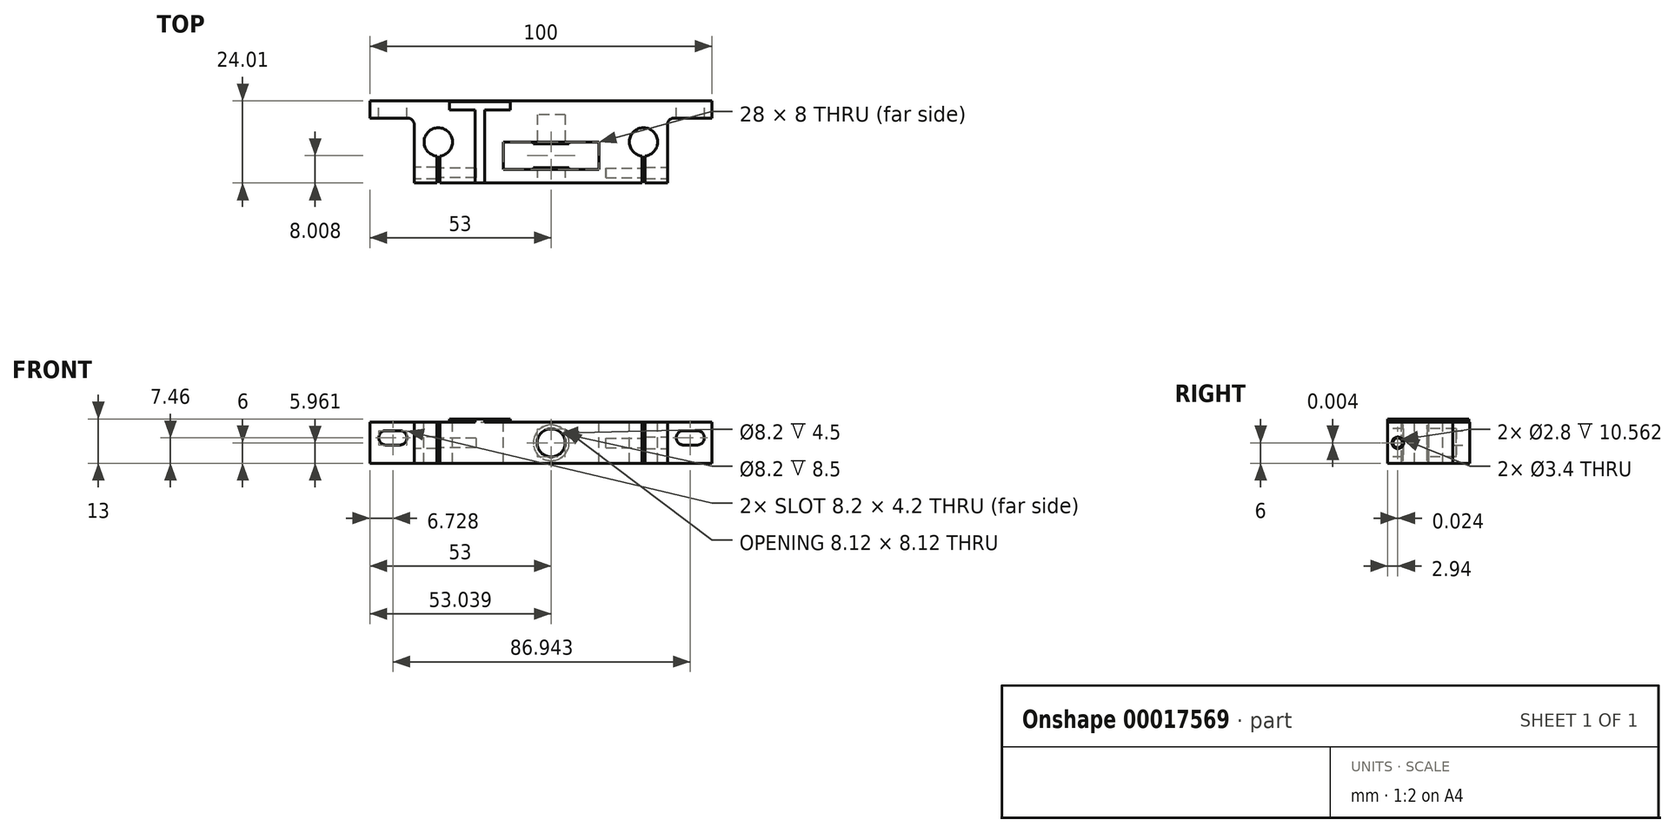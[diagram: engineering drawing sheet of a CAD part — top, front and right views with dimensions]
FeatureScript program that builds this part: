
annotation { "Feature Type Name" : "Feature", "Feature Type Description" : "" }
export const myFeature = defineFeature(function(context is Context, id is Id, definition is map)
    precondition{}
    {
        {
            var Q0;
            Q0=qCreatedBy(makeId("Top.planeOp"),FACE);
            var sketch = newSketch(context, id + "F0", { "sketchPlane" : qUnion([Q0])});
            skLineSegment(sketch, "E0", {"start": v(-46.35, 12.3) * mm, "end": v(53.65, 12.3) * mm});
            skLineSegment(sketch, "E1", {"start": v(53.65, 12.3) * mm, "end": v(53.65, 7.3) * mm});
            skLineSegment(sketch, "E2", {"start": v(53.65, 7.3) * mm, "end": v(40.65, 7.3) * mm});
            skLineSegment(sketch, "E3", {"start": v(40.65, 7.3) * mm, "end": v(40.65, -11.7) * mm});
            skLineSegment(sketch, "E4", {"start": v(40.65, -11.7) * mm, "end": v(-33.35, -11.7) * mm});
            skLineSegment(sketch, "E5", {"start": v(-33.35, -11.7) * mm, "end": v(-33.35, 7.3) * mm});
            skLineSegment(sketch, "E6", {"start": v(-33.35, 7.3) * mm, "end": v(-46.35, 7.3) * mm});
            skLineSegment(sketch, "E7", {"start": v(-46.35, 7.3) * mm, "end": v(-46.35, 12.3) * mm});
            skSolve(sketch);
        }
        {
            var Q0;
            Q0=qSketchRegion(id+"F0",true);
            extrude(context, id + "F1", {"entities" : qUnion([Q0]), "depth" : 12 * mm});
        }
        {
            var Q0;
            Q0=makeQuery(id+"F1.opExtrude","CAP_FACE",FACE,{"disambiguationData":[OSD([sQuery(id+"F0.wireOp",EDGE,"E0"),sQuery(id+"F0.wireOp",EDGE,"E1"),sQuery(id+"F0.wireOp",EDGE,"E2"),sQuery(id+"F0.wireOp",EDGE,"E3"),sQuery(id+"F0.wireOp",EDGE,"E4"),sQuery(id+"F0.wireOp",EDGE,"E5"),sQuery(id+"F0.wireOp",EDGE,"E6"),sQuery(id+"F0.wireOp",EDGE,"E7")])],"isStart":false});
            var sketch = newSketch(context, id + "F2", { "sketchPlane" : qUnion([Q0])});
            skCircle(sketch, "E8", {"center": v(-26.35, 0.3) * mm, "radius": 4.15 * mm});
            skCircle(sketch, "E9", {"center": v(33.65, 0.3) * mm, "radius": 4.15 * mm});
            skPoint(sketch, "E10", {"position": v(3.65, 12.3) * mm});
            skLineSegment(sketch, "E11.bottom", {"start": v(33.21, -3.01) * mm, "end": v(34.09, -3.01) * mm});
            skLineSegment(sketch, "E11.top", {"start": v(33.21, -12.27) * mm, "end": v(34.09, -12.27) * mm});
            skLineSegment(sketch, "E11.left", {"start": v(33.21, -3.01) * mm, "end": v(33.21, -12.27) * mm});
            skLineSegment(sketch, "E11.right", {"start": v(34.09, -3.01) * mm, "end": v(34.09, -12.27) * mm});
            skPoint(sketch, "E12", {"position": v(33.65, -3.01) * mm});
            skLineSegment(sketch, "E13", {"start": v(3.65, 12.3) * mm, "end": v(3.65, -11.7) * mm, "construction": true});
            skLineSegment(sketch, "E14.MirrorCS", {"start": v(-25.91, -12.27) * mm, "end": v(-26.79, -12.27) * mm});
            skLineSegment(sketch, "E15.MirrorCS", {"start": v(-26.79, -3.01) * mm, "end": v(-26.79, -12.27) * mm});
            skLineSegment(sketch, "E16.MirrorCS", {"start": v(-25.91, -3.01) * mm, "end": v(-26.79, -3.01) * mm});
            skLineSegment(sketch, "E17.MirrorCS", {"start": v(-25.91, -3.01) * mm, "end": v(-25.91, -12.27) * mm});
            skSolve(sketch);
        }
        {
            var Q0;
            Q0=qSketchRegion(id+"F2",true);
            var Q1;
            {var subQ3=sQuery(id+"F2.wireOp",EDGE,"E11.bottom");Q1=makeQuery(id+"F2.imprint","IMPRINT",FACE,{"disambiguationData":[TD([[makeQuery(id+"F2.imprint","IMPRINT",EDGE,{"derivedFrom":subQ3}),-1.0]])]});}
            var Q2;
            {var subQ3=sQuery(id+"F2.wireOp",EDGE,"E16.MirrorCS");Q2=makeQuery(id+"F2.imprint","IMPRINT",FACE,{"disambiguationData":[TD([[makeQuery(id+"F2.imprint","IMPRINT",EDGE,{"derivedFrom":subQ3}),1.0]])]});}
            extrude(context, id + "F3", {"entities" : qUnion([Q0, Q1, Q2]), "operationType" : NewBodyOperationType.REMOVE, "endBound" : BoundingType.THROUGH_ALL, "oppositeDirection" : true, "depth" : 25 * mm});
        }
        {
            var Q0;
            Q0=makeQuery(id+"F1.opExtrude","SWEPT_FACE",FACE,{"disambiguationData":[OSD([sQuery(id+"F0.wireOp",EDGE,"E0")])]});
            var sketch = newSketch(context, id + "F4", { "sketchPlane" : qUnion([Q0])});
            skLineSegment(sketch, "E18", {"start": v(-53.65, 7.46) * mm, "end": v(46.35, 7.46) * mm, "construction": true});
            skLineSegment(sketch, "E19.bottom", {"start": v(-49.32, 9.56) * mm, "end": v(-45.32, 9.56) * mm});
            skLineSegment(sketch, "E19.top", {"start": v(-49.32, 5.36) * mm, "end": v(-45.32, 5.36) * mm});
            skArc(sketch, "E20", {"start": v(-45.32, 5.36) * mm, "mid": v(-43.22, 7.46) * mm, "end": v(-45.32, 9.56) * mm});
            skArc(sketch, "E21", {"start": v(-49.32, 9.56) * mm, "mid": v(-51.42, 7.46) * mm, "end": v(-49.32, 5.36) * mm});
            skLineSegment(sketch, "E22.top", {"start": v(37.62, 5.36) * mm, "end": v(41.62, 5.36) * mm});
            skLineSegment(sketch, "E22.bottom", {"start": v(37.62, 9.56) * mm, "end": v(41.62, 9.56) * mm});
            skArc(sketch, "E23", {"start": v(37.62, 9.56) * mm, "mid": v(35.52, 7.46) * mm, "end": v(37.62, 5.36) * mm});
            skArc(sketch, "E24", {"start": v(41.62, 5.36) * mm, "mid": v(43.72, 7.46) * mm, "end": v(41.62, 9.56) * mm});
            skSolve(sketch);
        }
        {
            var Q0;
            Q0=qSketchRegion(id+"F4",true);
            extrude(context, id + "F5", {"entities" : qUnion([Q0]), "operationType" : NewBodyOperationType.REMOVE, "endBound" : BoundingType.THROUGH_ALL, "oppositeDirection" : true, "depth" : 25 * mm});
        }
        {
            var Q0;
            Q0=makeQuery(id+"F1.opExtrude","SWEPT_FACE",FACE,{"disambiguationData":[OSD([sQuery(id+"F0.wireOp",EDGE,"E4")])]});
            var sketch = newSketch(context, id + "F6", { "sketchPlane" : qUnion([Q0])});
            skLineSegment(sketch, "E25", {"start": v(-33.35, 6) * mm, "end": v(40.65, 6) * mm, "construction": true});
            skCircle(sketch, "E26", {"center": v(6.65, 6) * mm, "radius": 4.1 * mm});
            skSolve(sketch);
        }
        {
            var Q0;
            Q0=qSketchRegion(id+"F6",true);
            extrude(context, id + "F7", {"entities" : qUnion([Q0]), "operationType" : NewBodyOperationType.REMOVE, "oppositeDirection" : true, "depth" : 20 * mm});
        }
        {
            var Q0;
            Q0=makeQuery(id+"F1.opExtrude","CAP_FACE",FACE,{"disambiguationData":[OSD([sQuery(id+"F0.wireOp",EDGE,"E0"),sQuery(id+"F0.wireOp",EDGE,"E1"),sQuery(id+"F0.wireOp",EDGE,"E2"),sQuery(id+"F0.wireOp",EDGE,"E3"),sQuery(id+"F0.wireOp",EDGE,"E4"),sQuery(id+"F0.wireOp",EDGE,"E5"),sQuery(id+"F0.wireOp",EDGE,"E6"),sQuery(id+"F0.wireOp",EDGE,"E7")])],"isStart":false});
            var sketch = newSketch(context, id + "F8", { "sketchPlane" : qUnion([Q0])});
            skLineSegment(sketch, "E27.bottom", {"start": v(-7.35, 0.3) * mm, "end": v(20.65, 0.3) * mm});
            skLineSegment(sketch, "E27.top", {"start": v(-7.35, -7.7) * mm, "end": v(20.65, -7.7) * mm});
            skLineSegment(sketch, "E27.left", {"start": v(-7.35, 0.3) * mm, "end": v(-7.35, -7.7) * mm});
            skLineSegment(sketch, "E27.right", {"start": v(20.65, 0.3) * mm, "end": v(20.65, -7.7) * mm});
            skLineSegment(sketch, "E28", {"start": v(6.65, 12.3) * mm, "end": v(6.65, -11.7) * mm, "construction": true});
            skLineSegment(sketch, "E29", {"start": v(6.65, 0.3) * mm, "end": v(6.65, -7.7) * mm});
            skSolve(sketch);
        }
        {
            var Q0;
            Q0=qSketchRegion(id+"F8",true);
            extrude(context, id + "F9", {"entities" : qUnion([Q0]), "operationType" : NewBodyOperationType.REMOVE, "endBound" : BoundingType.THROUGH_ALL, "oppositeDirection" : true, "depth" : 25 * mm});
        }
        {
            var Q0;
            Q0=makeQuery(id+"F9.boolean.opBoolean","COPY",FACE,{"derivedFrom":makeQuery(id+"F9.opExtrude","SWEPT_FACE",FACE,{"disambiguationData":[OSD([sQuery(id+"F8.wireOp",EDGE,"E27.bottom")])]})});
            var sketch = newSketch(context, id + "F10", { "sketchPlane" : qUnion([Q0])});
            skCircle(sketch, "E30", {"center": v(6.65, 6) * mm, "radius": 5.2 * mm});
            skSolve(sketch);
        }
        {
            var Q0;
            Q0=makeQuery(id+"F10.imprint","IMPRINT",FACE,{"disambiguationData":[TD([[makeQuery(id+"F10.imprint","IMPRINT",EDGE,{"derivedFrom":sQuery(id+"F10.wireOp",EDGE,"E30")}),1.0]])]});
            extrude(context, id + "F11", {"entities" : qUnion([Q0]), "operationType" : NewBodyOperationType.ADD, "depth" : 0.5 * mm});
        }
        {
            var Q0;
            Q0=makeQuery(id+"F9.boolean.opBoolean","COPY",FACE,{"derivedFrom":makeQuery(id+"F9.opExtrude","SWEPT_FACE",FACE,{"disambiguationData":[OSD([sQuery(id+"F8.wireOp",EDGE,"E27.top")])]})});
            var sketch = newSketch(context, id + "F12", { "sketchPlane" : qUnion([Q0])});
            skCircle(sketch, "E31", {"center": v(-6.65, 6) * mm, "radius": 5.25 * mm});
            skSolve(sketch);
        }
        {
            var Q0;
            Q0=makeQuery(id+"F12.imprint","IMPRINT",FACE,{"disambiguationData":[TD([[makeQuery(id+"F12.imprint","IMPRINT",EDGE,{"derivedFrom":sQuery(id+"F12.wireOp",EDGE,"E31")}),1.0]])]});
            extrude(context, id + "F13", {"entities" : qUnion([Q0]), "operationType" : NewBodyOperationType.ADD, "depth" : 0.5 * mm});
        }
        {
            var Q0;
            Q0=makeQuery(id+"F1.opExtrude","CAP_FACE",FACE,{"disambiguationData":[OSD([sQuery(id+"F0.wireOp",EDGE,"E0"),sQuery(id+"F0.wireOp",EDGE,"E1"),sQuery(id+"F0.wireOp",EDGE,"E2"),sQuery(id+"F0.wireOp",EDGE,"E3"),sQuery(id+"F0.wireOp",EDGE,"E4"),sQuery(id+"F0.wireOp",EDGE,"E5"),sQuery(id+"F0.wireOp",EDGE,"E6"),sQuery(id+"F0.wireOp",EDGE,"E7")])],"isStart":false});
            var sketch = newSketch(context, id + "F14", { "sketchPlane" : qUnion([Q0])});
            skText(sketch, "E32", { "text": "T", "fontName": "OpenSans-Regular.ttf"});
            const initialGuessF14  = {"E32": [-0.02337, -0.0117, 1, 0, 0.024]};
            skSetInitialGuess(sketch, initialGuessF14);
            skSolve(sketch);
        }
        {
            var Q0;
            Q0=qSketchRegion(id+"F14",true);
            extrude(context, id + "F15", {"entities" : qUnion([Q0]), "operationType" : NewBodyOperationType.ADD, "depth" : 1 * mm});
        }
        {
            var Q0;
            Q0=makeQuery(id+"F1.opExtrude","SWEPT_FACE",FACE,{"disambiguationData":[OSD([sQuery(id+"F0.wireOp",EDGE,"E3")])]});
            var sketch = newSketch(context, id + "F16", { "sketchPlane" : qUnion([Q0])});
            skCircle(sketch, "E33", {"center": v(-8.74, 6) * mm, "radius": 1.7 * mm});
            skCircle(sketch, "E34", {"center": v(-8.74, 6) * mm, "radius": 1.4 * mm});
            skLineSegment(sketch, "E35", {"start": v(-11.7, 6) * mm, "end": v(-3.84, 6) * mm, "construction": true});
            skSolve(sketch);
        }
        {
            var Q0;
            Q0=makeQuery(id+"F16.imprint","IMPRINT",FACE,{"disambiguationData":[TD([[makeQuery(id+"F16.imprint","IMPRINT",EDGE,{"derivedFrom":sQuery(id+"F16.wireOp",EDGE,"E34")}),1.0]])]});
            extrude(context, id + "F17", {"entities" : qUnion([Q0]), "operationType" : NewBodyOperationType.REMOVE, "oppositeDirection" : true, "depth" : 18 * mm});
        }
        {
            var Q0;
            Q0=makeQuery(id+"F16.imprint","IMPRINT",FACE,{"disambiguationData":[TD([[makeQuery(id+"F16.imprint","IMPRINT",EDGE,{"derivedFrom":sQuery(id+"F16.wireOp",EDGE,"E34")}),1.0]])]});
            var Q1;
            Q1=makeQuery(id+"F16.imprint","IMPRINT",FACE,{"disambiguationData":[TD([[makeQuery(id+"F16.imprint","IMPRINT",EDGE,{"derivedFrom":sQuery(id+"F16.wireOp",EDGE,"E33")}),1.0]])]});
            extrude(context, id + "F18", {"entities" : qUnion([Q0, Q1]), "operationType" : NewBodyOperationType.REMOVE, "endBound" : BoundingType.UP_TO_NEXT, "oppositeDirection" : true, "depth" : 7 * mm});
        }
        {
            var Q0;
            Q0=makeQuery(id+"F1.opExtrude","SWEPT_EDGE",EDGE,{"disambiguationData":[OSD([sQuery(id+"F0.wireOp",EDGE,"E2"),sQuery(id+"F0.wireOp",EDGE,"E3")])]});
            fillet(context, id + "F19", {"entities" : qUnion([Q0]), "radius" : 2 * mm, "tangentPropagation" : true, "allowEdgeOverflow" : false});
        }
        {
            var Q0;
            Q0=makeQuery(id+"F1.opExtrude","SWEPT_FACE",FACE,{"disambiguationData":[OSD([sQuery(id+"F0.wireOp",EDGE,"E5")])]});
            var sketch = newSketch(context, id + "F20", { "sketchPlane" : qUnion([Q0])});
            skCircle(sketch, "E36", {"center": v(8.76, 6) * mm, "radius": 1.7 * mm});
            skCircle(sketch, "E37", {"center": v(8.76, 6) * mm, "radius": 1.4 * mm});
            skLineSegment(sketch, "E38", {"start": v(8.76, 0) * mm, "end": v(8.76, 12) * mm, "construction": true});
            skSolve(sketch);
        }
        {
            var Q0;
            Q0=makeQuery(id+"F20.imprint","IMPRINT",FACE,{"disambiguationData":[TD([[makeQuery(id+"F20.imprint","IMPRINT",EDGE,{"derivedFrom":sQuery(id+"F20.wireOp",EDGE,"E37")}),1.0]])]});
            extrude(context, id + "F21", {"entities" : qUnion([Q0]), "operationType" : NewBodyOperationType.REMOVE, "oppositeDirection" : true, "depth" : 18 * mm});
        }
        {
            var Q0;
            Q0=makeQuery(id+"F20.imprint","IMPRINT",FACE,{"disambiguationData":[TD([[makeQuery(id+"F20.imprint","IMPRINT",EDGE,{"derivedFrom":sQuery(id+"F20.wireOp",EDGE,"E37")}),1.0]])]});
            var Q1;
            Q1=makeQuery(id+"F20.imprint","IMPRINT",FACE,{"disambiguationData":[TD([[makeQuery(id+"F20.imprint","IMPRINT",EDGE,{"derivedFrom":sQuery(id+"F20.wireOp",EDGE,"E36")}),1.0]])]});
            extrude(context, id + "F22", {"entities" : qUnion([Q0, Q1]), "operationType" : NewBodyOperationType.REMOVE, "endBound" : BoundingType.UP_TO_NEXT, "oppositeDirection" : true, "depth" : 25 * mm});
        }
        {
            var Q0;
            Q0=makeQuery(id+"F1.opExtrude","SWEPT_EDGE",EDGE,{"disambiguationData":[OSD([sQuery(id+"F0.wireOp",EDGE,"E5"),sQuery(id+"F0.wireOp",EDGE,"E6")])]});
            fillet(context, id + "F23", {"entities" : qUnion([Q0]), "radius" : 2 * mm, "tangentPropagation" : true, "allowEdgeOverflow" : false});
        }
    });
